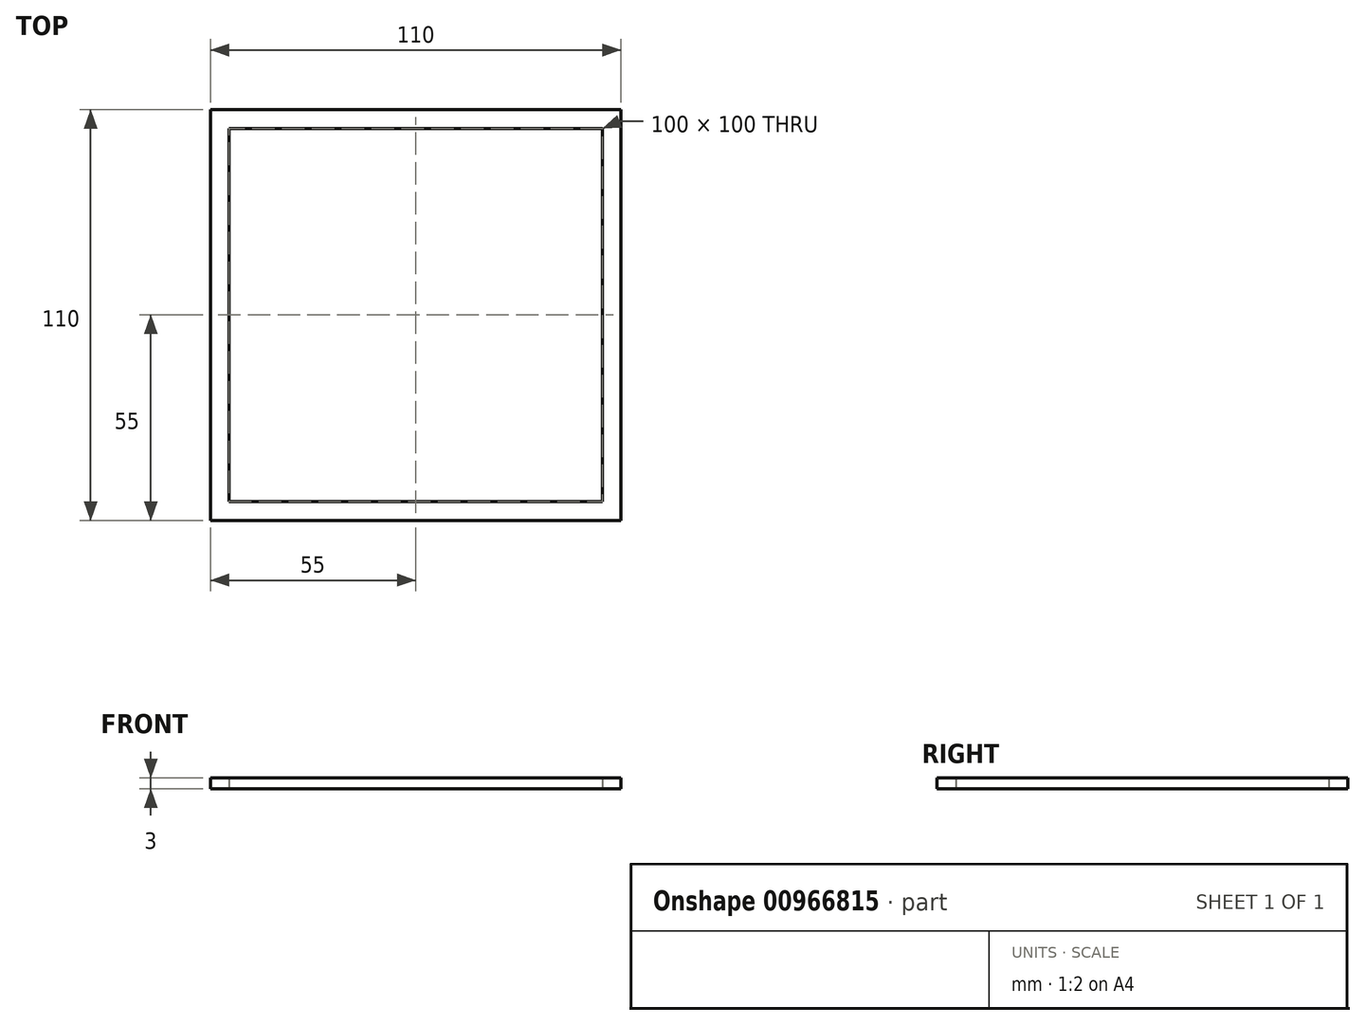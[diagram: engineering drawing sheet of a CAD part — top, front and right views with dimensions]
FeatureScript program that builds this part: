
annotation { "Feature Type Name" : "Feature", "Feature Type Description" : "" }
export const myFeature = defineFeature(function(context is Context, id is Id, definition is map)
    precondition{}
    {
        {
            var Q0;
            Q0=qCreatedBy(makeId("Top.planeOp"), FACE);
            var sketch = newSketch(context, id + "F0", { "sketchPlane" : qUnion([Q0])});
            skLineSegment(sketch, "E0.bottom", {"start": v(-50, 50) * mm, "end": v(50, 50) * mm});
            skLineSegment(sketch, "E0.top", {"start": v(-50, -50) * mm, "end": v(50, -50) * mm});
            skLineSegment(sketch, "E0.left", {"start": v(-50, 50) * mm, "end": v(-50, -50) * mm});
            skLineSegment(sketch, "E0.right", {"start": v(50, 50) * mm, "end": v(50, -50) * mm});
            skLineSegment(sketch, "E1.bottom", {"start": v(-55, 55) * mm, "end": v(55, 55) * mm});
            skLineSegment(sketch, "E1.top", {"start": v(-55, -55) * mm, "end": v(55, -55) * mm});
            skLineSegment(sketch, "E1.left", {"start": v(-55, 55) * mm, "end": v(-55, -55) * mm});
            skLineSegment(sketch, "E1.right", {"start": v(55, 55) * mm, "end": v(55, -55) * mm});
            skSolve(sketch);
        }
        {
            var Q0;
            Q0 = qSketchRegion(id + "F0", true);
            extrude(context, id + "F1", {"entities" : qUnion([Q0]), "domain" : OperationDomain.MODEL, "flatOperationType" : FlatOperationType.REMOVE, "depth" : 3 * mm, "offsetDistance" : 25 * mm});
        }
    });
